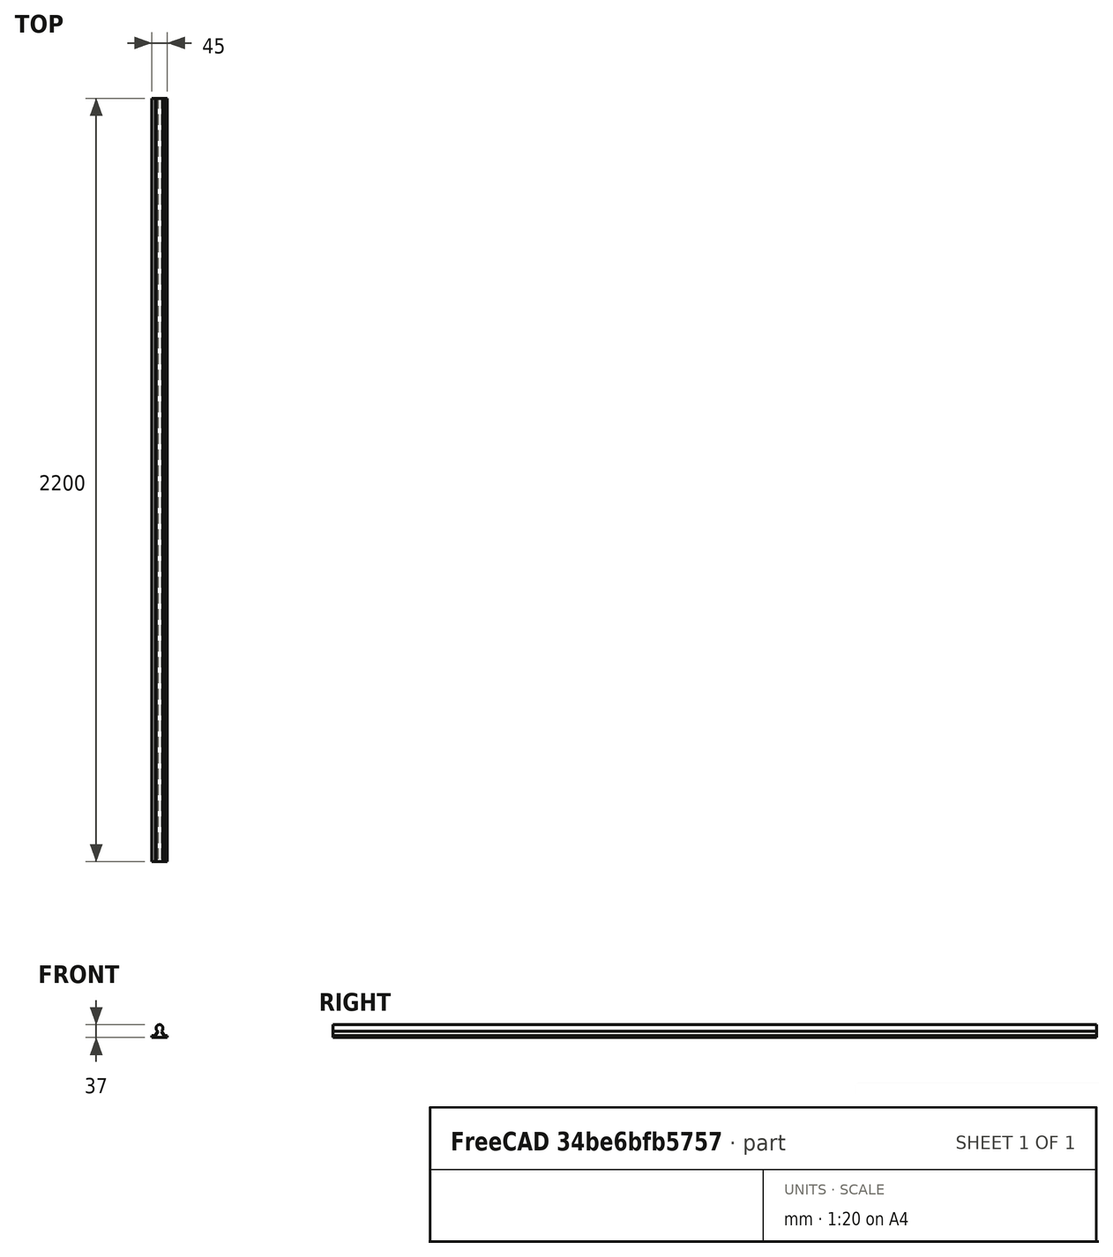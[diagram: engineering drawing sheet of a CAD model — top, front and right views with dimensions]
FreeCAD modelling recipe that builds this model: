
FCSTD DOCUMENT  (FreeCAD 1.0R39319 (Git))
Label: SBR20 2200mm rail
License: All rights reserved
LicenseURL: https://en.wikipedia.org/wiki/All_rights_reserved
objects: Sketcher::SketchObject×1, PartDesign::Pad×1, PartDesign::Body×1
note: 6 computed .brp shape members not serialized (recipe doc carries the construction recipe); baked Part::Feature solids carry a one-line shape summary decoded from their .brp

FEATURE [Sketcher::SketchObject] Sketch
  ArcFitTolerance = 1e-06
  AttachmentSupport = -> [XZ_Plane]
  FullyConstrained = true
  MakeInternals = false
  MapMode = 5
  Placement = pos=(0,0,0) rot=(1,0,0;1.5708rad)
  sketch-geometry (8):
    g0: ArcOfCircle CenterX=0 CenterY=0 CenterZ=0 NormalX=0 NormalY=0 NormalZ=1 AngleXU=0 Radius=10 StartAngle=5.23614 EndAngle=10.4721
    g1: LineSegment StartX=-22.5 StartY=-27 StartZ=0 EndX=22.5 EndY=-27 EndZ=0
    g2: LineSegment StartX=-22.5 StartY=-27 StartZ=0 EndX=-22.5 EndY=-22 EndZ=0
    g3: LineSegment StartX=22.5 StartY=-27 StartZ=0 EndX=22.5 EndY=-22 EndZ=0
    g4: LineSegment StartX=5.00128 StartY=-8.65952 StartZ=0 EndX=12.7034 EndY=-22 EndZ=0
    g5: LineSegment StartX=-4.99872 StartY=-8.66099 StartZ=0 EndX=-12.7 EndY=-22 EndZ=0
    g6: LineSegment StartX=-22.5 StartY=-22 StartZ=0 EndX=-12.7 EndY=-22 EndZ=0
    g7: LineSegment StartX=12.7034 StartY=-22 StartZ=0 EndX=22.5 EndY=-22 EndZ=0
  constraints (25):
    c: Diameter(g0) = 20
    c: Coincident(g0,g-1)
    c: Distance(g1) = 45
    c: Horizontal(g1)
    c: DistanceX(g1) = -22.5
    c: DistanceY(g1) = -27
    c: Distance(g2) = 5
    c: Coincident(g2,g1)
    c: Vertical(g2)
    c: Distance(g3) = 5
    c: Coincident(g3,g1)
    c: Vertical(g3)
    c: Angle(g-1,g4) = -1.0472
    c: Angle(g-1,g5) = -2.0944
    c: Coincident(g6,g2)
    c: Coincident(g7,g3)
    c: PointOnObject(g4,g7)
    c: Coincident(g0,g5)
    c: Coincident(g0,g4)
    c: Coincident(g6,g5)
    c: PointOnObject(g7,g4)
    c: DistanceX(g0,g0) = 10
    c: Horizontal(g6)
    c: Horizontal(g7)
    c: DistanceX(g6,g6) = 9.8
FEATURE [PartDesign::Pad] Pad
  Direction = (0,-1,2e-16)
  Length = 2200
  Length2 = 10
  Placement = pos=(0,0,0) rot=(1,0,0;1.5708rad)
  Profile = -> Sketch
  ReferenceAxis = -> Sketch [N_Axis]
  Refine = true
  Suppressed = false
  Type = 0
FEATURE [PartDesign::Body] Body
  AllowCompound = false
  Group = -> [Sketch,Pad]
  Origin = -> Origin
  Tip = -> Pad
